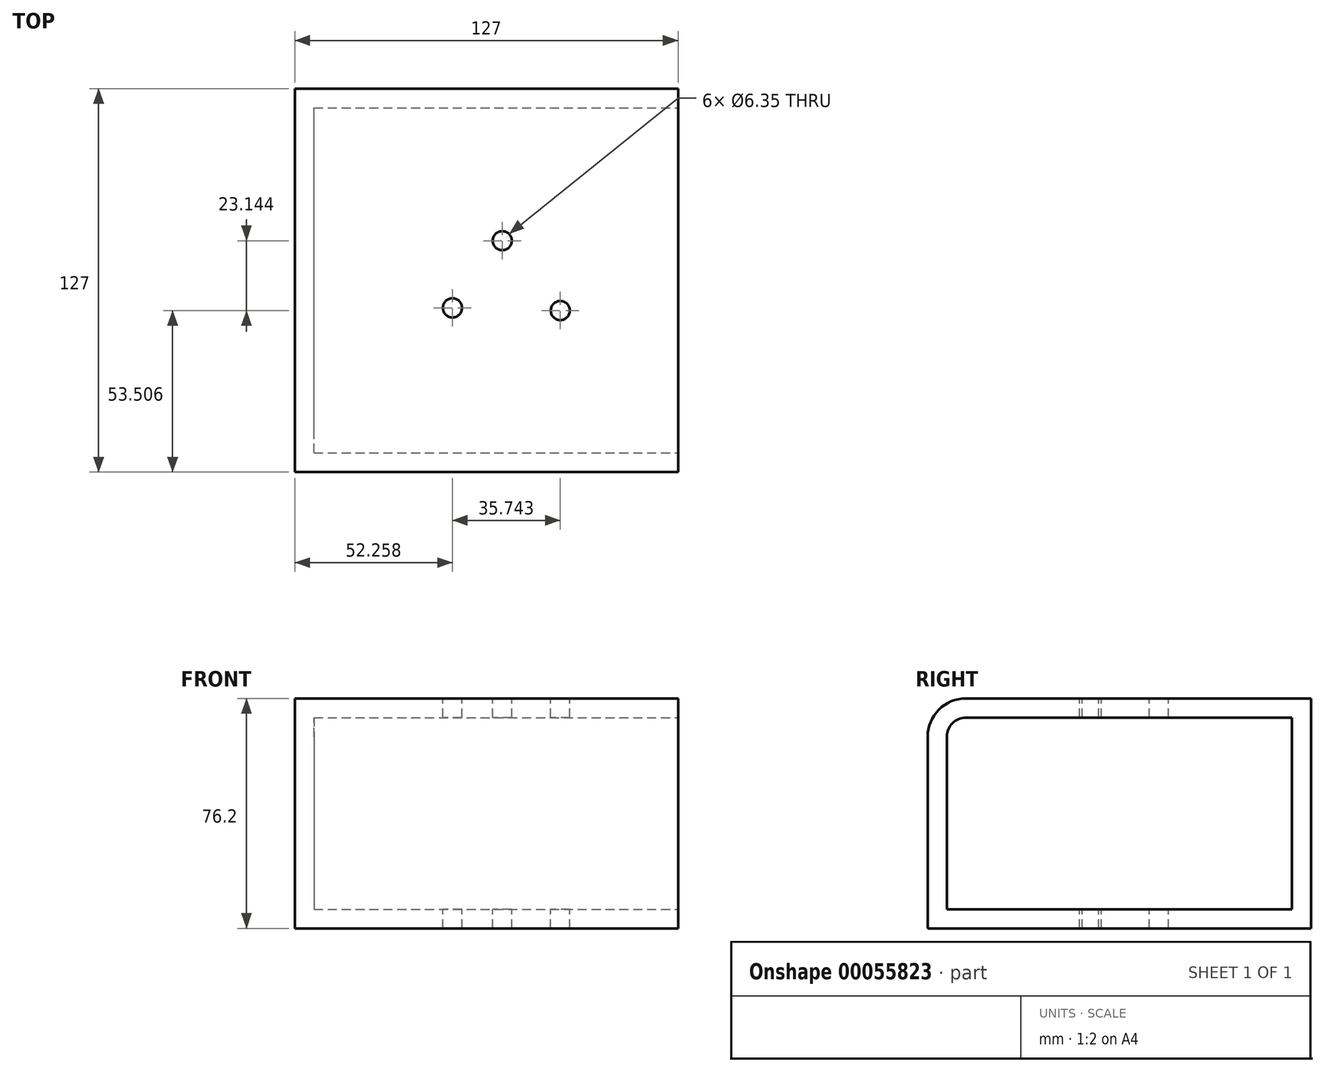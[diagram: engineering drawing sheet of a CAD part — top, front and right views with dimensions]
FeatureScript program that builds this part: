
annotation { "Feature Type Name" : "Feature", "Feature Type Description" : "" }
export const myFeature = defineFeature(function(context is Context, id is Id, definition is map)
    precondition{}
    {
        {
            var Q0;
            Q0=qCreatedBy(makeId("Top.planeOp"),FACE);
            var sketch = newSketch(context, id + "F0", { "sketchPlane" : qUnion([Q0])});
            skLineSegment(sketch, "E0.bottom", {"start": v(0, 0) * mm, "end": v(127, 0) * mm});
            skLineSegment(sketch, "E0.top", {"start": v(0, 127) * mm, "end": v(127, 127) * mm});
            skLineSegment(sketch, "E0.left", {"start": v(0, 0) * mm, "end": v(0, 127) * mm});
            skLineSegment(sketch, "E0.right", {"start": v(127, 0) * mm, "end": v(127, 127) * mm});
            skSolve(sketch);
        }
        {
            var Q0;
            Q0=makeQuery(id+"F0.imprint","IMPRINT",FACE,{"disambiguationData":[TD([[makeQuery(id+"F0.imprint","IMPRINT",EDGE,{"derivedFrom":sQuery(id+"F0.wireOp",EDGE,"E0.bottom")}),1.0]])]});
            extrude(context, id + "F1", {"entities" : qUnion([Q0]), "depth" : 76.2 * mm});
        }
        {
            var Q0;
            Q0=makeQuery(id+"F1.opExtrude","CAP_EDGE",EDGE,{"disambiguationData":[OSD([sQuery(id+"F0.wireOp",EDGE,"E0.bottom")])],"isStart":false});
            fillet(context, id + "F2", {"entities" : qUnion([Q0]), "radius" : 12.7 * mm, "tangentPropagation" : true, "allowEdgeOverflow" : false});
        }
        {
            var Q0;
            Q0=makeQuery(id+"F1.opExtrude","SWEPT_FACE",FACE,{"disambiguationData":[OSD([sQuery(id+"F0.wireOp",EDGE,"E0.right")])]});
            shell(context, id + "F3", {"entities" : qUnion([Q0]), "thickness" : 6.35 * mm});
        }
        {
            var Q0;
            Q0=makeQuery(id+"F1.opExtrude","CAP_FACE",FACE,{"disambiguationData":[OSD([sQuery(id+"F0.wireOp",EDGE,"E0.bottom"),sQuery(id+"F0.wireOp",EDGE,"E0.top"),sQuery(id+"F0.wireOp",EDGE,"E0.left"),sQuery(id+"F0.wireOp",EDGE,"E0.right")])],"isStart":false});
            var sketch = newSketch(context, id + "F4", { "sketchPlane" : qUnion([Q0])});
            skPoint(sketch, "E1", {"position": v(52.26, 54.4) * mm});
            skPoint(sketch, "E2", {"position": v(68.77, 76.65) * mm});
            skPoint(sketch, "E3", {"position": v(88, 53.5) * mm});
            skSolve(sketch);
        }
        {
            var Q0;
            Q0=sQuery(id+"F4.wireOp",VERTEX,"E1");
            var Q1;
            Q1=sQuery(id+"F4.wireOp",VERTEX,"E2");
            var Q2;
            Q2=sQuery(id+"F4.wireOp",VERTEX,"E3");
            var Q3;
            Q3=makeQuery(id+"F1.opExtrude","SWEPT_BODY",BODY,{"disambiguationData":[OSD([sQuery(id+"F0.wireOp",EDGE,"E0.bottom"),sQuery(id+"F0.wireOp",EDGE,"E0.top"),sQuery(id+"F0.wireOp",EDGE,"E0.left"),sQuery(id+"F0.wireOp",EDGE,"E0.right")])]});
            hole(context, id + "F5", {"style" : HoleStyle.SIMPLE, "holeDiameter" : 6.35 * mm, "endStyle" : HoleEndStyle.THROUGH, "locations" : qUnion([Q0, Q1, Q2]), "scope" : qUnion([Q3])});
        }
    });
